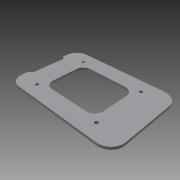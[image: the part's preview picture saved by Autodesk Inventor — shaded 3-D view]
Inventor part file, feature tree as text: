
AUTODESK INVENTOR PART (.ipt)
format: ipt  version: 2014 SP1 (Build 180222100, 222)  size: 109,056 bytes
history: native  units: mm
features: other x1, extrude x1, sketch x1
ambient origin geometry x8: Origin, YZ Plane, XZ Plane, XY Plane, X Axis, Y Axis, Z Axis, Center Point
bodies: Body1 (feature_tree)
feature tree (3):
  other  "Těleso1"
  extrude  "Vysunutí1"  Depth=65.0mm
  sketch  "Náčrt1"
